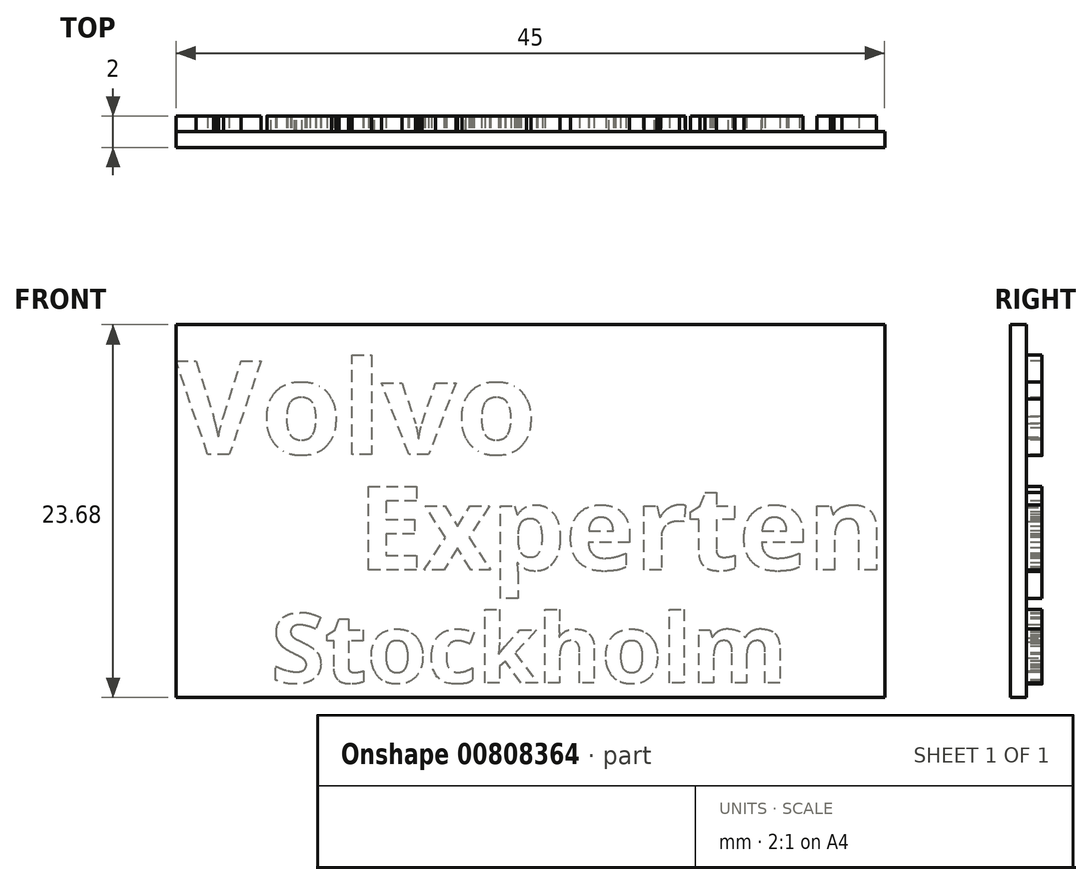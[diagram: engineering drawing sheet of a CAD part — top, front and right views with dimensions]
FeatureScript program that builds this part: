
annotation { "Feature Type Name" : "Feature", "Feature Type Description" : "" }
export const myFeature = defineFeature(function(context is Context, id is Id, definition is map)
    precondition{}
    {
        {
            var Q0;
            Q0=qCreatedBy(makeId("Front.planeOp"),FACE);
            var sketch = newSketch(context, id + "F0", { "sketchPlane" : qUnion([Q0])});
            skLineSegment(sketch, "E0.bottom", {"start": v(-6.38, 26.44) * mm, "end": v(38.62, 26.44) * mm});
            skLineSegment(sketch, "E0.top", {"start": v(-6.38, -8.56) * mm, "end": v(38.62, -8.56) * mm});
            skLineSegment(sketch, "E0.left", {"start": v(-6.38, 26.44) * mm, "end": v(-6.38, -8.56) * mm});
            skLineSegment(sketch, "E0.right", {"start": v(38.62, 26.44) * mm, "end": v(38.62, -8.56) * mm});
            skSolve(sketch);
        }
        {
            var Q0;
            Q0 = qSketchRegion(id + "F0", true);
            extrude(context, id + "F1", {"entities" : qUnion([Q0]), "depth" : 1 * mm, "offsetDistance" : 25.4 * mm});
        }
        {
            var Q0;
            Q0=makeQuery(id+"F1.opExtrude","CAP_FACE",FACE,{"disambiguationData":[OSD([sQuery(id+"F0.wireOp",EDGE,"E0.bottom"),sQuery(id+"F0.wireOp",EDGE,"E0.top"),sQuery(id+"F0.wireOp",EDGE,"E0.left"),sQuery(id+"F0.wireOp",EDGE,"E0.right")])],"isStart":false});
            var sketch = newSketch(context, id + "F2", { "sketchPlane" : qUnion([Q0])});
            skText(sketch, "E1", { "text": "Volvo\n", "fontName": "OpenSans-Bold.ttf"});
            skText(sketch, "E2", { "text": "Experten", "fontName": "OpenSans-Bold.ttf"});
            skText(sketch, "E3", { "text": "Stockholm\n", "fontName": "OpenSans-Bold.ttf"});
            const initialGuessF2  = {"E1": [-0.00638, 0.0182, 1, 0, 0.00597], "E2": [0.00516, 0.01085, 1, 0, 0.00536], "E3": [-0.00035, 0.00367, 1, 0, 0.00445]};
            skSetInitialGuess(sketch, initialGuessF2);
            skSolve(sketch);
        }
        {
            var Q0;
            Q0 = qSketchRegion(id + "F2", true);
            extrude(context, id + "F3", {"entities" : qUnion([Q0]), "operationType" : NewBodyOperationType.ADD, "depth" : 1 * mm, "offsetDistance" : 25.4 * mm});
        }
        {
            var Q0;
            {var subQ0=sQuery(id+"F0.wireOp",EDGE,"E0.left");var subQ1=sQuery(id+"F0.wireOp",EDGE,"E0.bottom");var subQ2=sQuery(id+"F0.wireOp",EDGE,"E0.right");var subQ3=sQuery(id+"F0.wireOp",EDGE,"E0.top");Q0=makeQuery(id+"F3.boolean.opBoolean","SPLIT",FACE,{"disambiguationData":[TD([makeQuery(id+"F1.opExtrude","SWEPT_FACE",FACE,{"disambiguationData":[OSD([subQ1])]})])],"derivedFrom":makeQuery(id+"F1.opExtrude","CAP_FACE",FACE,{"disambiguationData":[OSD([subQ1,subQ3,subQ0,subQ2])],"isStart":false})});}
            var sketch = newSketch(context, id + "F4", { "sketchPlane" : qUnion([Q0])});
            skLineSegment(sketch, "E4.bottom", {"start": v(-6.38, -8.56) * mm, "end": v(38.62, -8.56) * mm});
            skLineSegment(sketch, "E4.top", {"start": v(-6.38, 2.76) * mm, "end": v(38.62, 2.76) * mm});
            skLineSegment(sketch, "E4.left", {"start": v(-6.38, -8.56) * mm, "end": v(-6.38, 2.76) * mm});
            skLineSegment(sketch, "E4.right", {"start": v(38.62, -8.56) * mm, "end": v(38.62, 2.76) * mm});
            skSolve(sketch);
        }
        {
            var Q0;
            Q0 = qSketchRegion(id + "F4", true);
            extrude(context, id + "F5", {"entities" : qUnion([Q0]), "operationType" : NewBodyOperationType.REMOVE, "oppositeDirection" : true, "depth" : 25.4 * mm, "offsetDistance" : 25.4 * mm});
        }
        {
            var Q0;
            Q0=makeQuery(id+"F1.opExtrude","SWEPT_BODY",BODY,{"disambiguationData":[OSD([sQuery(id+"F0.wireOp",EDGE,"E0.bottom"),sQuery(id+"F0.wireOp",EDGE,"E0.top"),sQuery(id+"F0.wireOp",EDGE,"E0.left"),sQuery(id+"F0.wireOp",EDGE,"E0.right")])]});
            var Q1;
            Q1=qCreatedBy(makeId("Front.planeOp"),FACE);
            mirror(context, id + "F6", {"entities" : qUnion([Q0]), "mirrorPlane" : qUnion([Q1])});
        }
        {
            var Q0;
            Q0=makeQuery(id+"F3.opExtrude","CAP_FACE",FACE,{"disambiguationData":[OSD([sQuery(id+"F2.wireOp",EDGE,"E1.sketch_text.stroke-32"),sQuery(id+"F2.wireOp",EDGE,"E1.sketch_text.stroke-33"),sQuery(id+"F2.wireOp",EDGE,"E1.sketch_text.stroke-34"),sQuery(id+"F2.wireOp",EDGE,"E1.sketch_text.stroke-35"),sQuery(id+"F2.wireOp",EDGE,"E1.sketch_text.stroke-36"),sQuery(id+"F2.wireOp",EDGE,"E1.sketch_text.stroke-37"),sQuery(id+"F2.wireOp",EDGE,"E1.sketch_text.stroke-38"),sQuery(id+"F2.wireOp",EDGE,"E1.sketch_text.stroke-39"),sQuery(id+"F2.wireOp",EDGE,"E1.sketch_text.stroke-40"),sQuery(id+"F2.wireOp",EDGE,"E1.sketch_text.stroke-41")])],"isStart":false});
            var sketch = newSketch(context, id + "F7", { "sketchPlane" : qUnion([Q0])});
            skLineSegment(sketch, "E5", {"start": v(-7.33, 27.03) * mm, "end": v(40.64, 27.03) * mm});
            skLineSegment(sketch, "E6", {"start": v(40.64, 27.03) * mm, "end": v(40.64, 1.2) * mm});
            skLineSegment(sketch, "E7", {"start": v(40.64, 1.2) * mm, "end": v(-7.18, 1.2) * mm});
            skLineSegment(sketch, "E8", {"start": v(-7.18, 1.2) * mm, "end": v(-7.33, 27.03) * mm});
            skSolve(sketch);
        }
        {
            var Q0;
            Q0 = qSketchRegion(id + "F7", true);
            var Q1;
            Q1=makeQuery(id+"F6.opPattern","COPY",BODY,{"derivedFrom":makeQuery(id+"F1.opExtrude","SWEPT_BODY",BODY,{"disambiguationData":[OSD([sQuery(id+"F0.wireOp",EDGE,"E0.bottom"),sQuery(id+"F0.wireOp",EDGE,"E0.top"),sQuery(id+"F0.wireOp",EDGE,"E0.left"),sQuery(id+"F0.wireOp",EDGE,"E0.right")])]}),"instanceName":"1"});
            extrude(context, id + "F8", {"entities" : qUnion([Q0]), "operationType" : NewBodyOperationType.REMOVE, "oppositeDirection" : true, "depth" : 2 * mm, "endBoundEntityBody" : qUnion([Q1]), "offsetDistance" : 25.4 * mm});
        }
    });
